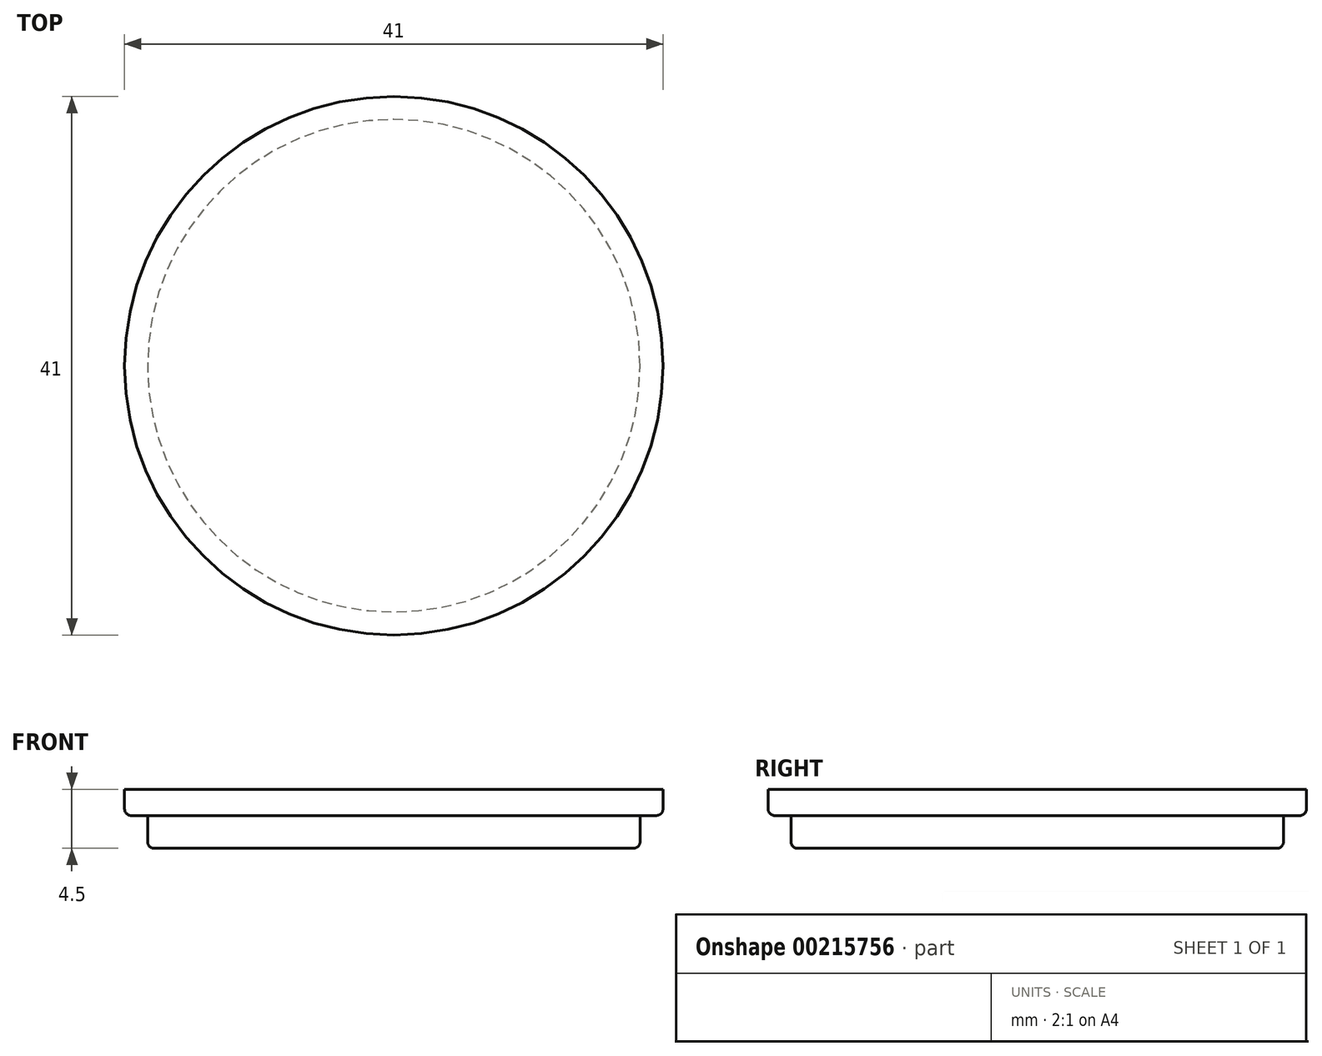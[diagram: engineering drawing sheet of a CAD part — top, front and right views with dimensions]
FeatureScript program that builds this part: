
annotation { "Feature Type Name" : "Feature", "Feature Type Description" : "" }
export const myFeature = defineFeature(function(context is Context, id is Id, definition is map)
    precondition{}
    {
        {
            var Q0;
            Q0=qCreatedBy(makeId("Top.planeOp"),FACE);
            var sketch = newSketch(context, id + "F0", { "sketchPlane" : qUnion([Q0])});
            skCircle(sketch, "E0", {"center": v(0, 0) * mm, "radius": 18.75 * mm});
            skSolve(sketch);
        }
        {
            var Q0;
            Q0 = qSketchRegion(id + "F0", true);
            extrude(context, id + "F1", {"entities" : qUnion([Q0]), "depth" : 2.5 * mm});
        }
        {
            var Q0;
            Q0=makeQuery(id+"F1.opExtrude","CAP_EDGE",EDGE,{"disambiguationData":[OSD([sQuery(id+"F0.wireOp",EDGE,"E0")])],"isStart":true});
            fillet(context, id + "F2", {"entities" : qUnion([Q0]), "radius" : 0.5 * mm, "tangentPropagation" : true, "allowEdgeOverflow" : false});
        }
        {
            var Q0;
            Q0=makeQuery(id+"F1.opExtrude","CAP_FACE",FACE,{"disambiguationData":[OSD([sQuery(id+"F0.wireOp",EDGE,"E0")])],"isStart":false});
            var sketch = newSketch(context, id + "F3", { "sketchPlane" : qUnion([Q0])});
            skCircle(sketch, "E1", {"center": v(0, 0) * mm, "radius": 20.5 * mm});
            skSolve(sketch);
        }
        {
            var Q0;
            Q0 = qSketchRegion(id + "F3", true);
            extrude(context, id + "F4", {"entities" : qUnion([Q0]), "operationType" : NewBodyOperationType.ADD, "depth" : 2 * mm});
        }
        {
            var Q0;
            Q0=makeQuery(id+"F4.opExtrude","CAP_EDGE",EDGE,{"disambiguationData":[OSD([sQuery(id+"F3.wireOp",EDGE,"E1")])],"isStart":true});
            fillet(context, id + "F5", {"entities" : qUnion([Q0]), "radius" : 0.5 * mm, "tangentPropagation" : true, "allowEdgeOverflow" : false});
        }
    });
